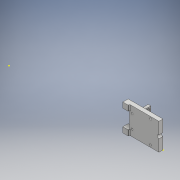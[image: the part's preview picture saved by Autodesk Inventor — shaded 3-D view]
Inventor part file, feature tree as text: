
AUTODESK INVENTOR PART (.ipt)
format: ipt  version: 2018 (Build 220112000, 112)  size: 629,248 bytes
history: native  units: mm
features: sketch x33, extrude x25, fillet x8, hole x6
ambient origin geometry x8: Origin, YZ Plane, XZ Plane, XY Plane, X Axis, Y Axis, Z Axis, Center Point
bodies: Solid1 (feature_tree)
feature tree (72):
  extrude  "Extrusion1"  Depth=50.0mm
  hole  "Hole1"  [1 undecoded]
  hole  "Hole2"  [1 undecoded]
  extrude  "Extrusion2"  Depth=25.0mm
  extrude  "Extrusion3"  Depth=25.0mm
  extrude  "Extrusion4"  Depth=5.0mm
  sketch  "Sketch7"  dims[d25=10.0mm d26=5.0mm]
  extrude  "Extrusion5"  Depth=5.0mm
  extrude  "Extrusion6"  Depth=17.5mm
  extrude  "Extrusion7"  Depth=35.0mm
  extrude  "Extrusion8"  Depth=35.0mm
  extrude  "Extrusion9"  Depth=2.0mm TaperAngle=0.0deg
  extrude  "Extrusion10"  Depth=7.5mm TaperAngle=0.0deg
  extrude  "Extrusion11"  Depth=10.0mm
  extrude  "Extrusion12"  Depth=7.5mm
  fillet  "Fillet1"  Radius=7.5mm
  fillet  "Fillet2"  Radius=25.0mm
  fillet  "Fillet3"  Radius=3.0mm
  fillet  "Fillet4"  Radius=3.2mm
  fillet  "Fillet5"  Radius=2.1mm
  fillet  "Fillet6"  Radius=5.5mm
  extrude  "Extrusion13"  Depth=92.5mm TaperAngle=0.0deg
  sketch  "Sketch17"  dims[d58=4.25mm d59=241.0mm d60=0.0mm]
  hole  "Hole3"  [1 undecoded]
  hole  "Hole4"  [1 undecoded]
  extrude  "Extrusion14"  Depth=5.0mm
  extrude  "Extrusion15"  Depth=2.5mm TaperAngle=0.0deg
  extrude  "Extrusion16"  Depth=30.0mm
  extrude  "Extrusion17"  Depth=2.5mm
  extrude  "Extrusion18"  Depth=14.55mm TaperAngle=0.0deg
  extrude  "Extrusion19"  Depth=0.1mm
  extrude  "Extrusion20"  Depth=3.25mm
  extrude  "Extrusion21"  Depth=3.25mm
  hole  "Hole5"  [1 undecoded]
  extrude  "Extrusion22"  Depth=2.0mm
  extrude  "Extrusion23"  Depth=15.0mm
  extrude  "Extrusion24"  Depth=10.0mm TaperAngle=0.0deg
  extrude  "Extrusion25"  Depth=2.0mm
  fillet  "Fillet7"  Radius=100.0mm
  fillet  "Fillet8"  Radius=100.0mm
  hole  "Hole6"  [1 undecoded]
  sketch  "Sketch1"  dims[d0=50.0mm d1=50.0mm]
  sketch  "Sketch2"  dims[d2=240.0mm d3=7.5mm]
  sketch  "Sketch3"  dims[d4=7.5mm d5=7.5mm d6=0.0mm]
  sketch  "Sketch4"  dims[d7=6.35mm d8=6.0mm d9=4.0mm d10=2.0mm d11=90.0deg d12=8.0mm d13=20.594885mm d14=25.0mm]
  sketch  "Sketch5"  dims[d15=3.3mm d16=6.0mm d17=4.0mm d18=2.0mm d19=90.0deg d20=8.0mm d21=20.594885mm d22=25.0mm]
  sketch  "Sketch6"  dims[d23=180.0deg d24=5.0mm]
  sketch  "Sketch8"  dims[d27=17.5mm d28=0.0mm d30=35.0mm]
  sketch  "Sketch9"  dims[d31=35.0mm d32=35.0mm]
  sketch  "Sketch10"  dims[d33=35.0mm d34=35.0mm]
  sketch  "Sketch11"  dims[d35=35.0mm d36=2.0mm d37=0.0mm]
  sketch  "Sketch12"  dims[d38=10.0mm d39=7.5mm d40=0.0mm]
  sketch  "Sketch13"  dims[d41=100.0mm d42=10.0mm]
  sketch  "Sketch14"  dims[d43=7.5mm d44=0.0mm d45=7.5mm d46=7.5mm d47=25.0mm d48=0.0mm d49=3.0mm d50=3.2mm d51=2.1mm d52=5.5mm]
  sketch  "Sketch15"  dims[d53=3.3mm d54=92.5mm d55=0.0mm]
  sketch  "Sketch16"  dims[d56=5.5mm d57=3.3mm]
  sketch  "Sketch18"  dims[d61=4.44mm d62=5.0mm]
  sketch  "Sketch19"  dims[d63=2.5mm d64=91.25mm d65=0.0mm]
  sketch  "Sketch20"  dims[d66=30.0mm d67=6.35mm]
  sketch  "Sketch21"  dims[d68=3.8mm d69=0.0mm d70=2.5mm]
  sketch  "Sketch22"  dims[d71=14.55mm d72=0.0mm d73=14.55mm d74=0.0mm]
  sketch  "Sketch23"  dims[d75=0.1mm d76=0.1mm]
  sketch  "Sketch24"  dims[d77=3.25mm d78=3.25mm]
  sketch  "Sketch25"  dims[d79=3.25mm d80=3.25mm]
  sketch  "Sketch26"  dims[d81=35.0mm d82=10.0mm]
  sketch  "Sketch27"  dims[d83=2.0mm d84=0.0mm d85=3.6mm]
  sketch  "Sketch28"  dims[d86=3.6mm]
  sketch  "Sketch29"  dims[d87=3.3mm d88=6.0mm d89=4.0mm d90=2.0mm d91=90.0deg d92=15.0mm d93=20.594885mm]
  sketch  "Sketch30"  dims[d94=3.3mm d95=6.0mm d96=4.0mm d97=2.0mm d98=90.0deg d99=15.0mm d100=20.594885mm d101=6.0mm]
  sketch  "Sketch31"  dims[d102=20.0mm d103=0.0mm d104=10.0mm d105=0.0mm]
  sketch  "Sketch32"  dims[d106=2.0mm d107=0.0mm d108=4.0mm d109=100.0mm d110=0.0mm d111=100.0mm d112=0.0mm]
  sketch  "Sketch33"  dims[d113=5.0mm d114=2.0mm d115=0.0mm d116=3.3mm d117=3.3mm d118=3.3mm d119=3.3mm d120=2.0mm d121=0.0mm d122=5.5mm d123=0.0mm d124=3.3mm d125=6.0mm d126=4.0mm d127=2.0mm d128=90.0deg d129=8.0mm d130=20.594885mm d131=42.0mm d132=17.0mm d133=21.0mm d135=8.5mm d136=15.825mm d137=3.5mm d138=21.0mm d139=3.3mm d140=3.3mm d141=3.3mm d142=10.0mm d143=0.0mm d144=7.5mm d145=0.0mm d146=100.0mm d147=0.0mm d148=10.0mm d149=10.0mm d150=10.0mm d151=10.0mm d152=10.0mm d153=0.0mm d154=2.0mm d155=2.0mm d156=6.25mm d157=6.0mm d158=4.0mm d159=2.0mm d160=90.0deg d161=8.0mm d162=0.0mm]
note: 6 required parameter values undecoded (feature->parameter linkage not recoverable at this tier; creation-order binding heuristic only, values carry confidence <= 0.55)
